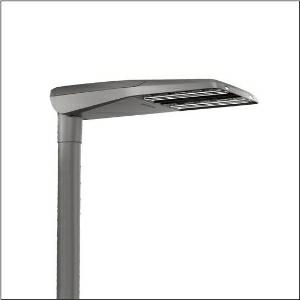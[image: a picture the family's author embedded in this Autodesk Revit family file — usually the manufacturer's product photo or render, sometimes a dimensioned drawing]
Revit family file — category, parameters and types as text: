
# Revit family: streetlight_sl_11_iq_midi___st1_2a_5xc3a51e08me_cf1e
name_source: partatom
category: Lighting Fixtures
units: mm (PartAtom-declared; Revit-internal decimal feet)

## family parameters
Cut with Voids When Loaded = No
Host = Face
Light Source = No
Part Type = Normal
Room Calculation Point = No
Round Connector Dimension = Use Diameter
Shared = No

## types (1)
- --- (1 x LED, 18110 lm, 124.7 W, 3000K)
    Apparent Load = 125 VA
    CIE Flux Codes = 32 70 96 100 100
    Color Rendering = 70
    Color Temperature = 3000K
    Default Elevation = 1800 mm
    Description = Streetlight SL 11 iQ midi, mast luminaire, primary light control with 3 zone facetted reflector, of plastic, silver coated, highly specular, primary optical cover: cover, of PMMA, transparent, light distribution: ST1.2a, light emission: direct distribution, primary light characteristic: asymmetric, installation type: post-top, side-entry, lamps: LED, High Power LED, rated values: 18.110lm | 124,7W | 145,2lm/W (begin service life); end service life: 18.110lm | 132,2W; at 50% lumin. flux: 9.055lm | 57,2W | 158,3lm/W, colour temperature: 3000K, colour rendering: CRI > 70, light colour: 730, light setting 1 begin service life: 100% | 18.110lm | 124,7W | 145,2lm/W | 3.000K, light setting 1 end service life: 132,2W, further light settings possible, control: optimised constant luminous flux control (CLO 2.0), Desk-Remote (wireless, voltage-free reading and setting of iQ features in the workshop via application-optimized NFC function/RFID function), Light-Fading, Smart-Wire, Night-Set, Lumen-Switch, Temp-Guard, Auto-Match, with cable H07RN-F 3x 1.5mm², mains connection: 230..240V, AC, 50/60Hz, connection cable pre-assembled, cable length: 12,5m, luminaire housing, of diecast aluminium, powder-coated, SITECO metallic grey (DB 702S), please order mast flange separately, inclination adjustable without tools: 0°, 5°, 10°, 15° (post-top) | 0°, -5°, -10°, -15° (side-entry), sealing non-destructively replaceable, multi-level sealing system, length: 780mm, width: 376mm, height: 118mm, mast flange for spigot size: 42mm (side-entry): 5XC10008XM4, 60/48mm (side-entry/post-top): 5XC10108XM2, 76/60mm (side-entry/post-top): 5XC10108XM1, equipment: Power, protection rating (complete): IP66, insulation class (complete): insulation class II (safety insulation), certification: CE, ENEC, ENEC+, VDE, impact resistance: IK10, permissible operating ambient temperature for outdoor applications: -25..+50°C, standard-compliant lighting for roads and squares, Environmental Product Declaration (EPD) tested and certified by an independent institute, packaging unit: 1 piece

Light Distribution: ST1.2a
    Height = 118 mm
    Lamp = 1 x LED
    Lamp Light Flux = 18110 lm
    Lamp Power = 124.7 W
    Lamp count = 1
    Length = 780 mm
    Luminous efficacy = 145 lm/W
    Manufacturer = Siteco
    ModVariant = No
    Model = 5XC3A51E08ME
    Number of Poles = 1
    OnlyDefault = Yes
    Power Factor = 1
    Product Name = Streetlight SL 11 iQ midi | ST1.2a
    Product group = mast luminaire | pylon top
    ProductGroupID = 6100
    Protection Class = Protection class II
    Protection Degree = IP 66
    RLX_Detail_Level = 1
    RLX_Emergency_Light_Flux = 0 lm
    RLX_Emergency_Type = 0
    RLX_Emergency_Type_DB = No
    RlxData = <blob elided: 70981 chars, md5=66dea245>
    Socket = socket
    Standby Power = 0 W
    System Light Flux = 18110 lm
    System Power = 125 W
    Type Comments = factory setting: luminous flux: 100 % | dim-lin: 254 | 557 mA
    Type Image = l_1005960.jpg
    URL = http://relux.com
    VarID = @adj_193725
    Voltage = 0 V
    Weight = 0.00 kg
    Width = 376 mm

## geometry (parser evidence)
native form markers: Blend x4, Sweep x10
no freeform markers — native parametric forms only
